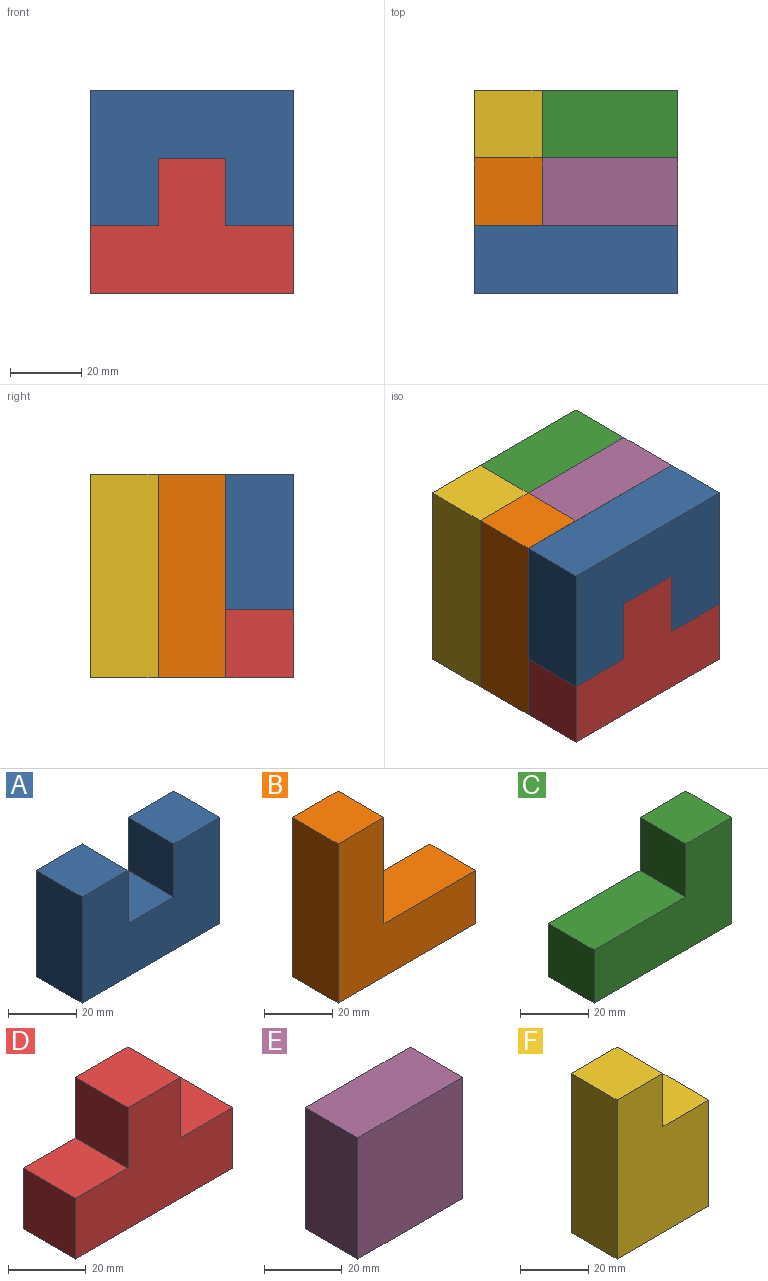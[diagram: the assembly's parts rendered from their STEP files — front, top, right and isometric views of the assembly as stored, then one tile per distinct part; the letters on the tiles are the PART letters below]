
ASSEMBLY  parts=6 mates=5
PART A: 10 faces, bbox 57.2x19.1x38.1 mm
  f0: plane 38.1x19.05mm, normal (-1,0,0), area 725.8mm2, adj f1,f7,f8,f9
  f1: plane 57.15x19.05mm, normal (0,0,-1), area 1088.7mm2, adj f0,f2,f8,f9
  f2: plane 38.1x19.05mm, normal (1,0,0), area 725.8mm2, adj f1,f3,f8,f9
  f3: plane 19.05x19.05mm, normal (0,0,1), area 362.9mm2, adj f2,f4,f8,f9
  f4: plane 19.05x19.05mm, normal (-1,0,0), area 362.9mm2, adj f3,f5,f8,f9
  f5: plane 19.05x19.05mm, normal (0,0,1), area 362.9mm2, adj f4,f6,f8,f9
  f6: plane 19.05x19.05mm, normal (1,0,0), area 362.9mm2, adj f5,f7,f8,f9
  f7: plane 19.05x19.05mm, normal (0,0,1), area 362.9mm2, adj f0,f6,f8,f9
  f8: plane 57.15x38.1mm, normal (0,-1,0), area 1814.5mm2, adj f0,f1,f2,f3,f4,f5,f6,f7
  f9: plane 57.15x38.1mm, normal (0,1,0), area 1814.5mm2, adj f0,f1,f2,f3,f4,f5,f6,f7
PART B: 8 faces, bbox 57.2x19.1x57.2 mm
  f0: plane 57.15x19.05mm, normal (-1,0,0), area 1088.7mm2, adj f1,f5,f6,f7
  f1: plane 57.15x19.05mm, normal (0,0,-1), area 1088.7mm2, adj f0,f2,f6,f7
  f2: plane 19.05x19.05mm, normal (1,0,0), area 362.9mm2, adj f1,f3,f6,f7
  f3: plane 38.1x19.05mm, normal (0,0,1), area 725.8mm2, adj f2,f4,f6,f7
  f4: plane 38.1x19.05mm, normal (1,0,0), area 725.8mm2, adj f3,f5,f6,f7
  f5: plane 19.05x19.05mm, normal (0,0,1), area 362.9mm2, adj f0,f4,f6,f7
  f6: plane 57.15x57.15mm, normal (0,-1,0), area 1814.5mm2, adj f0,f1,f2,f3,f4,f5
  f7: plane 57.15x57.15mm, normal (0,1,0), area 1814.5mm2, adj f0,f1,f2,f3,f4,f5
PART C: 8 faces, bbox 57.2x19.1x38.1 mm
  f0: plane 57.15x19.05mm, normal (0,0,-1), area 1088.7mm2, adj f1,f5,f6,f7
  f1: plane 38.1x19.05mm, normal (1,0,0), area 725.8mm2, adj f0,f2,f6,f7
  f2: plane 19.05x19.05mm, normal (0,0,1), area 362.9mm2, adj f1,f3,f6,f7
  f3: plane 19.05x19.05mm, normal (-1,0,0), area 362.9mm2, adj f2,f4,f6,f7
  f4: plane 38.1x19.05mm, normal (0,0,1), area 725.8mm2, adj f3,f5,f6,f7
  f5: plane 19.05x19.05mm, normal (-1,0,0), area 362.9mm2, adj f0,f4,f6,f7
  f6: plane 57.15x38.1mm, normal (0,-1,0), area 1451.6mm2, adj f0,f1,f2,f3,f4,f5
  f7: plane 57.15x38.1mm, normal (0,1,0), area 1451.6mm2, adj f0,f1,f2,f3,f4,f5
PART D: 10 faces, bbox 57.2x19.1x38.1 mm
  f0: plane 57.15x19.05mm, normal (0,0,-1), area 1088.7mm2, adj f1,f7,f8,f9
  f1: plane 19.05x19.05mm, normal (1,0,0), area 362.9mm2, adj f0,f2,f8,f9
  f2: plane 19.05x19.05mm, normal (0,0,1), area 362.9mm2, adj f1,f3,f8,f9
  f3: plane 19.05x19.05mm, normal (1,0,0), area 362.9mm2, adj f2,f4,f8,f9
  f4: plane 19.05x19.05mm, normal (0,0,1), area 362.9mm2, adj f3,f5,f8,f9
  f5: plane 19.05x19.05mm, normal (-1,0,0), area 362.9mm2, adj f4,f6,f8,f9
  f6: plane 19.05x19.05mm, normal (0,0,1), area 362.9mm2, adj f5,f7,f8,f9
  f7: plane 19.05x19.05mm, normal (-1,0,0), area 362.9mm2, adj f0,f6,f8,f9
  f8: plane 57.15x38.1mm, normal (0,-1,0), area 1451.6mm2, adj f0,f1,f2,f3,f4,f5,f6,f7
  f9: plane 57.15x38.1mm, normal (0,1,0), area 1451.6mm2, adj f0,f1,f2,f3,f4,f5,f6,f7
PART E: 6 faces, bbox 38.1x19.1x38.1 mm
  f0: plane 38.1x19.05mm, normal (0,0,-1), area 725.8mm2, adj f1,f3,f4,f5
  f1: plane 38.1x19.05mm, normal (1,0,0), area 725.8mm2, adj f0,f2,f4,f5
  f2: plane 38.1x19.05mm, normal (0,0,1), area 725.8mm2, adj f1,f3,f4,f5
  f3: plane 38.1x19.05mm, normal (-1,0,0), area 725.8mm2, adj f0,f2,f4,f5
  f4: plane 38.1x38.1mm, normal (0,-1,0), area 1451.6mm2, adj f0,f1,f2,f3
  f5: plane 38.1x38.1mm, normal (0,1,0), area 1451.6mm2, adj f0,f1,f2,f3
PART F: 8 faces, bbox 38.1x19.1x57.2 mm
  f0: plane 57.15x19.05mm, normal (-1,0,0), area 1088.7mm2, adj f1,f5,f6,f7
  f1: plane 38.1x19.05mm, normal (0,0,-1), area 725.8mm2, adj f0,f2,f6,f7
  f2: plane 38.1x19.05mm, normal (1,0,0), area 725.8mm2, adj f1,f3,f6,f7
  f3: plane 19.05x19.05mm, normal (0,0,1), area 362.9mm2, adj f2,f4,f6,f7
  f4: plane 19.05x19.05mm, normal (1,0,0), area 362.9mm2, adj f3,f5,f6,f7
  f5: plane 19.05x19.05mm, normal (0,0,1), area 362.9mm2, adj f0,f4,f6,f7
  f6: plane 57.15x38.1mm, normal (0,-1,0), area 1814.5mm2, adj f0,f1,f2,f3,f4,f5
  f7: plane 57.15x38.1mm, normal (0,1,0), area 1814.5mm2, adj f0,f1,f2,f3,f4,f5
PLACE A rot(axis=(0,1,0),180deg) t=(114.71,-91.94,42.89)mm
PLACE B t=(54.34,-72.89,-25.41)mm
PLACE C rot(axis=(0,-1,0),90deg) t=(111.49,-53.84,-22.08)mm
PLACE D t=(47.43,-91.94,-14.26)mm
PLACE E t=(73.39,-72.89,-6.72)mm
PLACE F rot(axis=(0,1,0),0deg) t=(49.8,-53.84,-14.26)mm
MATE fastened E.f0 <-> B.f3  axis (0,0,-1) through (73.39,-91.94,4.79)mm
MATE fastened F.f3 <-> C.f3  axis (0,0,1) through (73.39,-72.89,23.84)mm
MATE fastened E.f5 <-> C.f6  axis (0,1,0) through (111.49,-72.89,42.89)mm
MATE fastened A.f9 <-> B.f6  axis (0,1,0) through (54.34,-91.94,42.89)mm
MATE fastened A.f5 <-> D.f4  axis (0,0,-1) through (92.44,-110.99,23.84)mm
